# Revit family: PRD_FrankeWS_TltRllHldrs_RODANToiletRollHolder_RODX678
name_source: partatom
category: Specialty Equipment
revit_build: Autodesk Revit 2018 (Build: 20190510_1515(x64)
units: mm (PartAtom-declared; Revit-internal decimal feet)

## family parameters
Cut with Voids When Loaded = No
Host = Face
OmniClass Number = 23.40.20.21.21
OmniClass Title = Toilet Paper Dispensers
Part Type = Normal
Room Calculation Point = No
Round Connector Dimension = Use Diameter
Shared = No

## types (1)
- RODX678
    AssetType = Fixed
    BIMObjectName = PRD_AR_ToiletRollHolders_RODANToiletRollHolder_RODX678
    Category = Pr_40_20_76_88, Toilet roll holders
    Default Elevation = 600 mm
    Description = Toilet roll holder for wall mounting, stainless steel, surface satin finished, material thickness 0.8 mm, folding cover, for 1 roll with max. diameter 130 mm, inclusive stainless steel screws and dowels.
    DurationUnit = year
    Features = stainless steel, surface satin finished
    FillingQuantity = 1
    FillingQuantityUom = Rolls
    Finish = satin finished
    GrossWeight = 0.38 kg
    HolderMaterial = PRD_AR_StainlessSteel_SatinFinished
    IfcExportAs = IfcFurnitureType
    IfcExportType = USERDEFINED
    IntegralAccessories = incl. stainless steel screws and dowels
    IsBuiltIn = TRUE
    Lock = No lock
    MainColor = stainless steel
    Manufacturer = KWC Group AG
    ManufacturerName = KWC Group AG
    ManufacturerURL = www.kwc.com
    Material = stainless steel
    MaterialCode = 1.4301
    MaterialThickness = 0.80 mm
    MaximumDepthDiameterOfConsumable = 150.00 mm
    MaximumWidthOfConsumable = 130.00 mm
    Model = RODX678
    ModelNumber = 2030013026
    ModelReference = RODX678
    NBSDescription = Toilet roll holders
    NBSReference = 45-35-72/368
    Name = Toilet roll holder RODX678
    NetWeight = 0.30 kg
    NominalDepth = 30 mm  [stored 0.0984252 ft]
    NominalHeight = 130 mm  [stored 0.426509 ft]
    NominalWidth = 135 mm  [stored 0.442913 ft]
    ProductInformation = https://pim.kwc.com
    Size = 135 x 130 x 25 mm
    Spindle = Yes
    Style = Roll holder
    ToiletRollMaterial = PRD_AR_ToiletRoll
    TypeOfFixing = Screw
    TypeOfMounting = Wall mounting
    URL = www.kwc.com
    Uniclass2015Code = Pr_40_20_76_88
    Uniclass2015Title = Toilet roll holders
    Uniclass2015Version = Products v1.17
    Version = 1
    WarrantyDurationUnit = year

note: [stored X ft] marks values corroborated as IEEE doubles in the binary element streams (Revit-internal decimal feet)

## geometry (parser evidence)
native form markers: Sweep x1
no freeform markers — native parametric forms only
